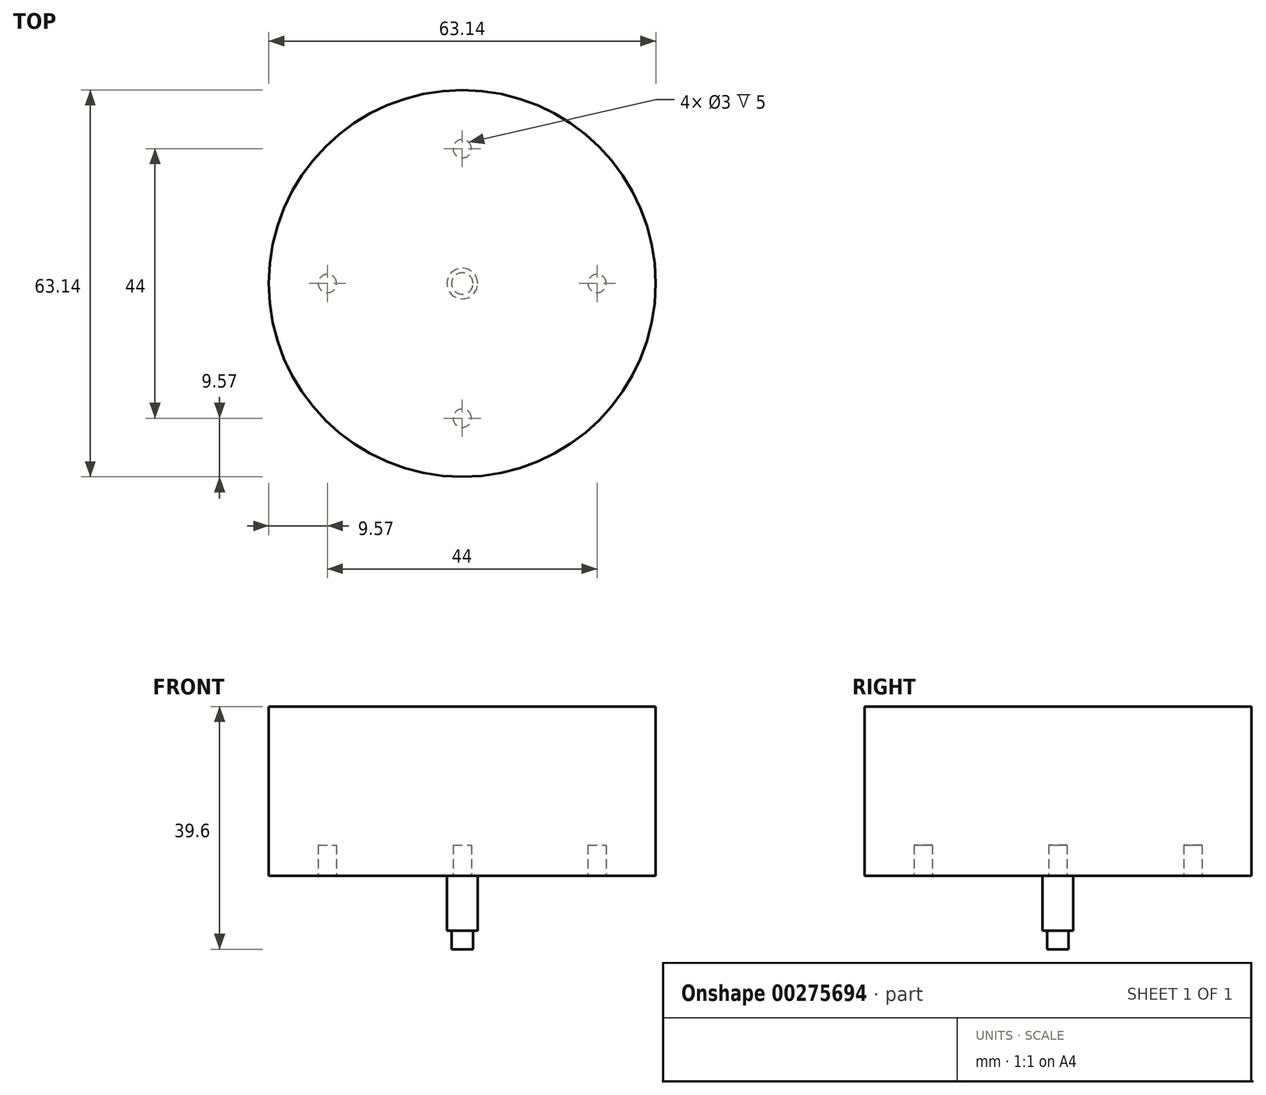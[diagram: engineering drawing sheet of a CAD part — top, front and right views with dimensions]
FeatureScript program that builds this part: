
annotation { "Feature Type Name" : "Feature", "Feature Type Description" : "" }
export const myFeature = defineFeature(function(context is Context, id is Id, definition is map)
    precondition{}
    {
        {
            var Q0;
            Q0=qCreatedBy(makeId("Top.planeOp"),FACE);
            var sketch = newSketch(context, id + "F0", { "sketchPlane" : qUnion([Q0])});
            skCircle(sketch, "E0", {"center": v(0, 0) * mm, "radius": 31.57 * mm});
            skSolve(sketch);
        }
        {
            var Q0;
            Q0 = qSketchRegion(id + "F0", true);
            extrude(context, id + "F1", {"entities" : qUnion([Q0]), "depth" : 27.6 * mm});
        }
        {
            var Q0;
            Q0=makeQuery(id+"F1.opExtrude","CAP_FACE",FACE,{"disambiguationData":[OSD([sQuery(id+"F0.wireOp",EDGE,"E0")])],"isStart":true});
            var sketch = newSketch(context, id + "F2", { "sketchPlane" : qUnion([Q0])});
            skCircle(sketch, "E1", {"center": v(0, 0) * mm, "radius": 2.5 * mm});
            skSolve(sketch);
        }
        {
            var Q0;
            Q0 = qSketchRegion(id + "F2", true);
            extrude(context, id + "F3", {"entities" : qUnion([Q0]), "operationType" : NewBodyOperationType.ADD, "depth" : 9 * mm});
        }
        {
            var Q0;
            Q0=makeQuery(id+"F3.opExtrude","CAP_FACE",FACE,{"disambiguationData":[OSD([sQuery(id+"F2.wireOp",EDGE,"E1")])],"isStart":false});
            var sketch = newSketch(context, id + "F4", { "sketchPlane" : qUnion([Q0])});
            skCircle(sketch, "E2", {"center": v(0, 0) * mm, "radius": 1.75 * mm});
            skSolve(sketch);
        }
        {
            var Q0;
            Q0 = qSketchRegion(id + "F4", true);
            extrude(context, id + "F5", {"entities" : qUnion([Q0]), "operationType" : NewBodyOperationType.ADD, "depth" : 3 * mm});
        }
        {
            var Q0;
            Q0=makeQuery(id+"F1.opExtrude","CAP_FACE",FACE,{"disambiguationData":[OSD([sQuery(id+"F0.wireOp",EDGE,"E0")])],"isStart":true});
            var sketch = newSketch(context, id + "F6", { "sketchPlane" : qUnion([Q0])});
            skLineSegment(sketch, "E3", {"start": v(0, 0) * mm, "end": v(0, 73.25) * mm, "construction": true});
            skCircle(sketch, "E4", {"center": v(0, 22) * mm, "radius": 1.5 * mm});
            skCircle(sketch, "E5.MirrorC", {"center": v(0, -22) * mm, "radius": 1.5 * mm});
            skCircle(sketch, "E6.1.0", {"center": v(-22, 0) * mm, "radius": 1.5 * mm});
            skCircle(sketch, "E6.3.0", {"center": v(22, 0) * mm, "radius": 1.5 * mm});
            skPoint(sketch, "E6.center", {"position": v(0, 0) * mm});
            skSolve(sketch);
        }
        {
            var Q0;
            Q0 = qSketchRegion(id + "F6", true);
            extrude(context, id + "F7", {"entities" : qUnion([Q0]), "operationType" : NewBodyOperationType.REMOVE, "oppositeDirection" : true, "depth" : 5 * mm});
        }
    });
